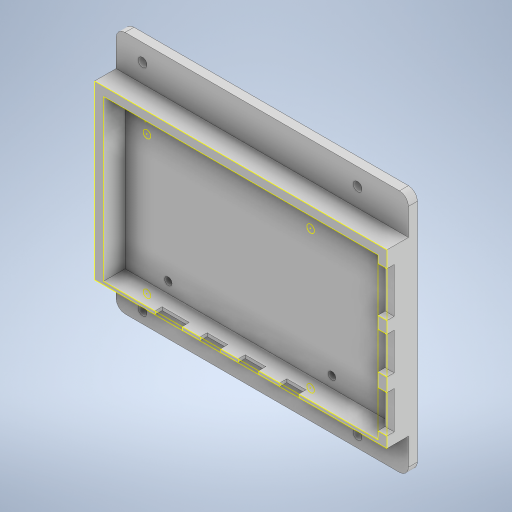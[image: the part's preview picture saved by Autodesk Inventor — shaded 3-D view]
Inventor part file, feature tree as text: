
AUTODESK INVENTOR PART (.ipt)
format: ipt  version: 2024 (Build 280153000, 153)  size: 499,712 bytes
history: native  units: in
note: dims shown in document units (in); Inventor stores cm internally (conversion verified against a paired STEP export)
features: projected_geometry x16, extrude x4, sketch x4
ambient origin geometry x8: Origin, YZ Plane, XZ Plane, XY Plane, X Axis, Y Axis, Z Axis, Center Point
bodies: Solid1 (feature_tree)
feature tree (24):
  extrude  "Extrusion1"  Depth=0.125in
  extrude  "Extrusion2"  Depth=0.015in
  extrude  "Extrusion3"  Depth=0.015in
  extrude  "Extrusion4"  Depth=0.125in
  sketch  "Sketch7"  dims[d7=0.015in d8=0.125in d9=0.3in d10=0.0in d11=0.5in d12=0.5in d13=0.125in d14=0.125in d15=1.5in d16=3.0in d17=1.5in d18=3.0in d19=1.5in d20=3.0in d21=0.125in d22=0.125in d23=0.125in d24=0.125in d25=0.125in d26=0.0in d27=0.0in d28=0.0in d30=0.2in d31=0.0in]
  sketch  "Sketch3"  dims[d0=0.5906in d2=0.125in]
  sketch  "Sketch4"  dims[d3=0.015in d4=0.015in]
  sketch  "Sketch6"  dims[d5=0.015in d6=0.015in]
  projected_geometry  "Projected Loop1"
  projected_geometry  "Projected Loop2"
  projected_geometry  "Projected Loop3"
  projected_geometry  "Projected Loop4"
  projected_geometry  "Projected Loop5"
  projected_geometry  "Projected Loop6"
  projected_geometry  "Projected Loop7"
  projected_geometry  "Projected Loop8"
  projected_geometry  "Projected Loop9"
  projected_geometry  "Projected Loop10"
  projected_geometry  "Projected Loop11"
  projected_geometry  "Projected Loop12"
  projected_geometry  "Projected Loop13"
  projected_geometry  "Projected Loop14"
  projected_geometry  "Projected Loop15"
  projected_geometry  "Projected Loop16"
